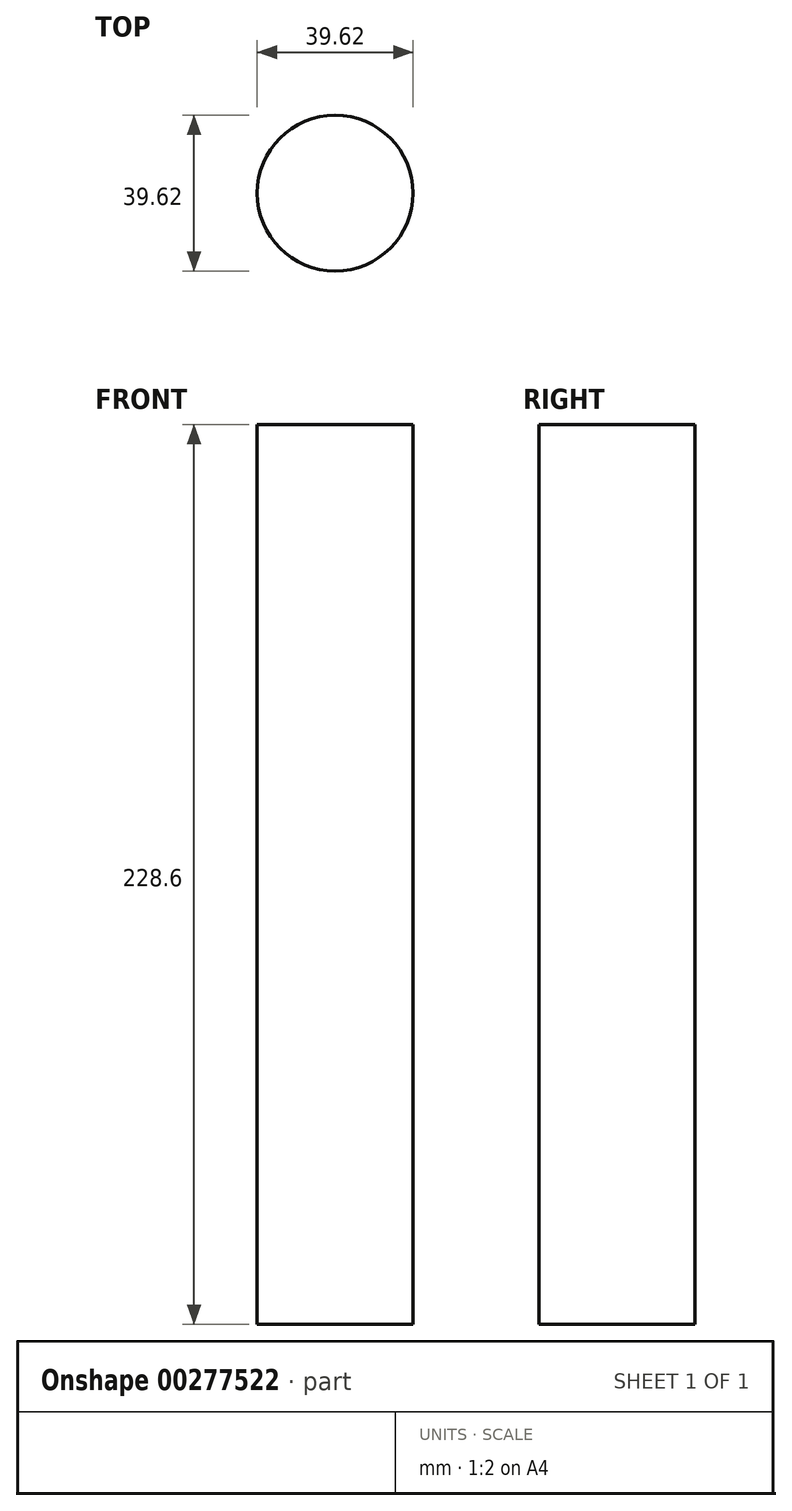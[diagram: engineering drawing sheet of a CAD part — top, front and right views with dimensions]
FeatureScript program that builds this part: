
annotation { "Feature Type Name" : "Feature", "Feature Type Description" : "" }
export const myFeature = defineFeature(function(context is Context, id is Id, definition is map)
    precondition{}
    {
        {
            var Q0;
            Q0=qCreatedBy(makeId("Top.planeOp"),FACE);
            var sketch = newSketch(context, id + "F0", { "sketchPlane" : qUnion([Q0])});
            skCircle(sketch, "E0", {"center": v(0, 0) * mm, "radius": 19.81 * mm});
            skSolve(sketch);
        }
        {
            var Q0;
            Q0=makeQuery(id+"F0.imprint","IMPRINT",FACE,{"disambiguationData":[TD([[makeQuery(id+"F0.imprint","IMPRINT",EDGE,{"derivedFrom":sQuery(id+"F0.wireOp",EDGE,"E0")}),1.0]])]});
            extrude(context, id + "F1", {"entities" : qUnion([Q0]), "depth" : 228.6 * mm});
        }
    });
